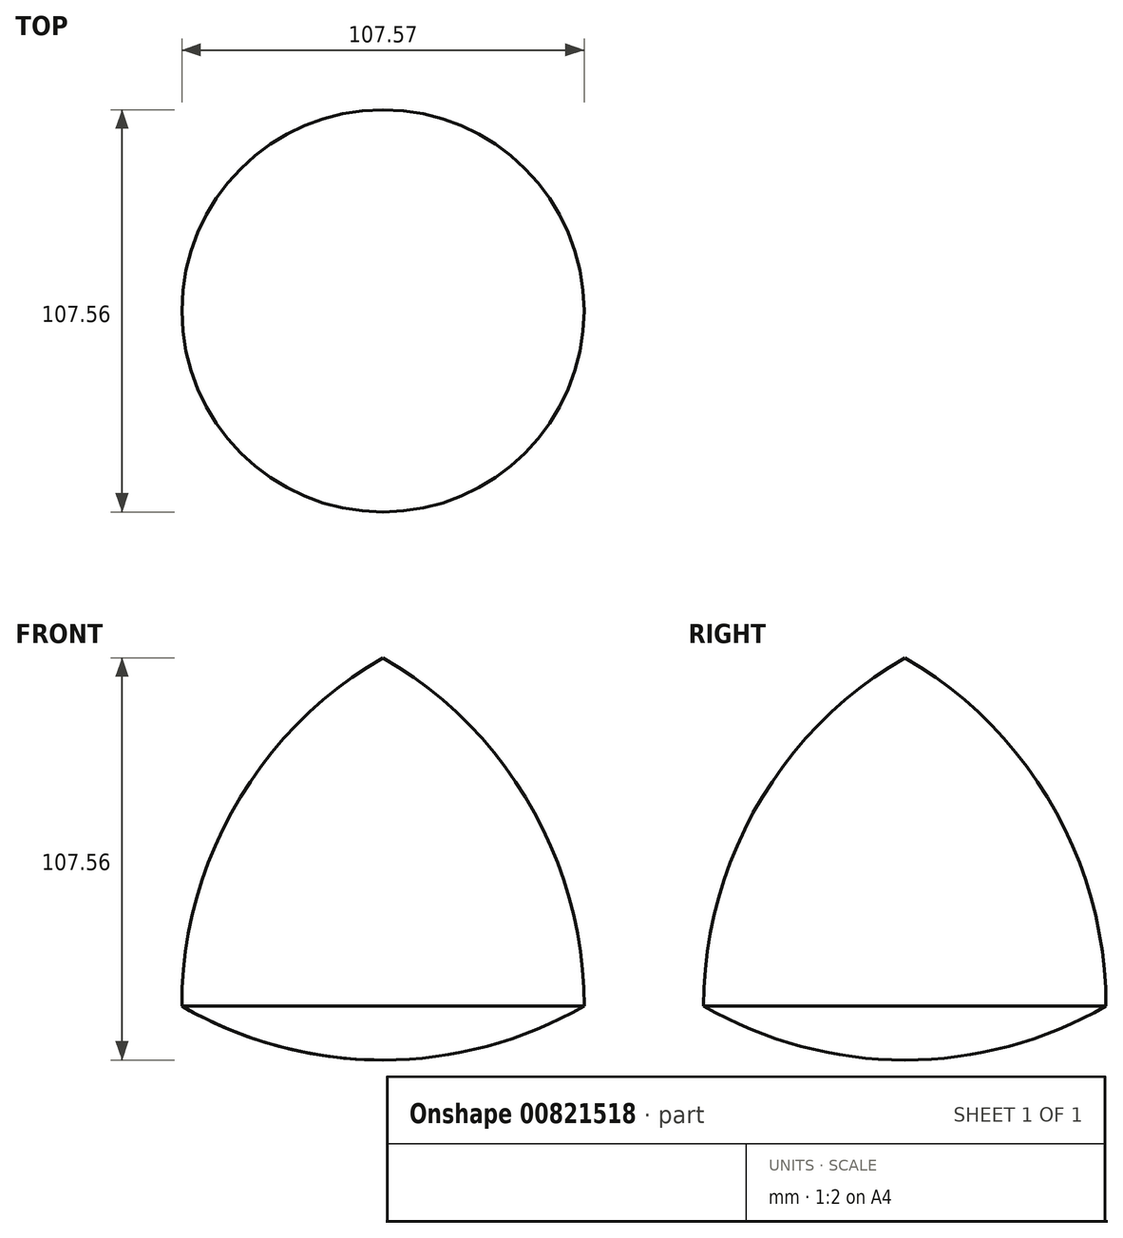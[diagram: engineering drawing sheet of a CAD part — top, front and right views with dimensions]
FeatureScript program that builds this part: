
annotation { "Feature Type Name" : "Feature", "Feature Type Description" : "" }
export const myFeature = defineFeature(function(context is Context, id is Id, definition is map)
    precondition{}
    {
        {
            var Q0;
            Q0=qCreatedBy(makeId("Front.planeOp"),FACE);
            var sketch = newSketch(context, id + "F0", { "sketchPlane" : qUnion([Q0])});
            skLineSegment(sketch, "E0", {"start": v(0, 0) * mm, "end": v(107.57, 0) * mm});
            skLineSegment(sketch, "E1", {"start": v(107.57, 0) * mm, "end": v(107.57, 0) * mm});
            skLineSegment(sketch, "E2", {"start": v(53.78, 93.15) * mm, "end": v(0, 0) * mm});
            skLineSegment(sketch, "E3", {"start": v(53.78, 93.15) * mm, "end": v(107.57, 0) * mm});
            skArc(sketch, "E4", {"start": v(0, 0) * mm, "mid": v(53.78, -14.41) * mm, "end": v(107.57, 0) * mm});
            skArc(sketch, "E5", {"start": v(53.78, 93.15) * mm, "mid": v(14.41, 53.78) * mm, "end": v(0, 0) * mm});
            skArc(sketch, "E6", {"start": v(107.57, 0) * mm, "mid": v(93.15, 53.78) * mm, "end": v(53.78, 93.15) * mm});
            skLineSegment(sketch, "E7", {"start": v(53.78, 93.15) * mm, "end": v(53.78, -71.7) * mm});
            skSolve(sketch);
        }
        {
            var Q0;
            Q0=makeQuery(id+"F0.imprint","IMPRINT",FACE,{"disambiguationData":[TD([[makeQuery(id+"F0.imprint","IMPRINT",EDGE,{"derivedFrom":sQuery(id+"F0.wireOp",EDGE,"E2")}),-1.0]])]});
            var Q1;
            {var subQ1=sQuery(id+"F0.wireOp",EDGE,"E2");Q1=makeQuery(id+"F0.imprint","IMPRINT",FACE,{"disambiguationData":[TD([[makeQuery(id+"F0.imprint","IMPRINT",EDGE,{"derivedFrom":subQ1}),1.0]])]});}
            var Q2;
            {var subQ0=sQuery(id+"F0.wireOp",EDGE,"E4");var subQ3=sQuery(id+"F0.wireOp",EDGE,"E7");var subQ5=makeQuery(id+"F0.imprint","INTERSECT",VERTEX,{"derivedFrom":[subQ0,subQ3]});Q2=makeQuery(id+"F0.imprint","IMPRINT",FACE,{"disambiguationData":[TD([[makeQuery(id+"F0.imprint","IMPRINT",EDGE,{"disambiguationData":[TD([[subQ5,1.0]])],"derivedFrom":subQ3}),-1.0]])]});}
            var Q3;
            Q3=sQuery(id+"F0.wireOp",EDGE,"E7");
            revolve(context, id + "F1", {"surfaceOperationType" : NewSurfaceOperationType.NEW, "entities" : qUnion([Q0, Q1, Q2]), "axis" : qUnion([Q3]), "revolveType" : RevolveType.FULL});
        }
    });
